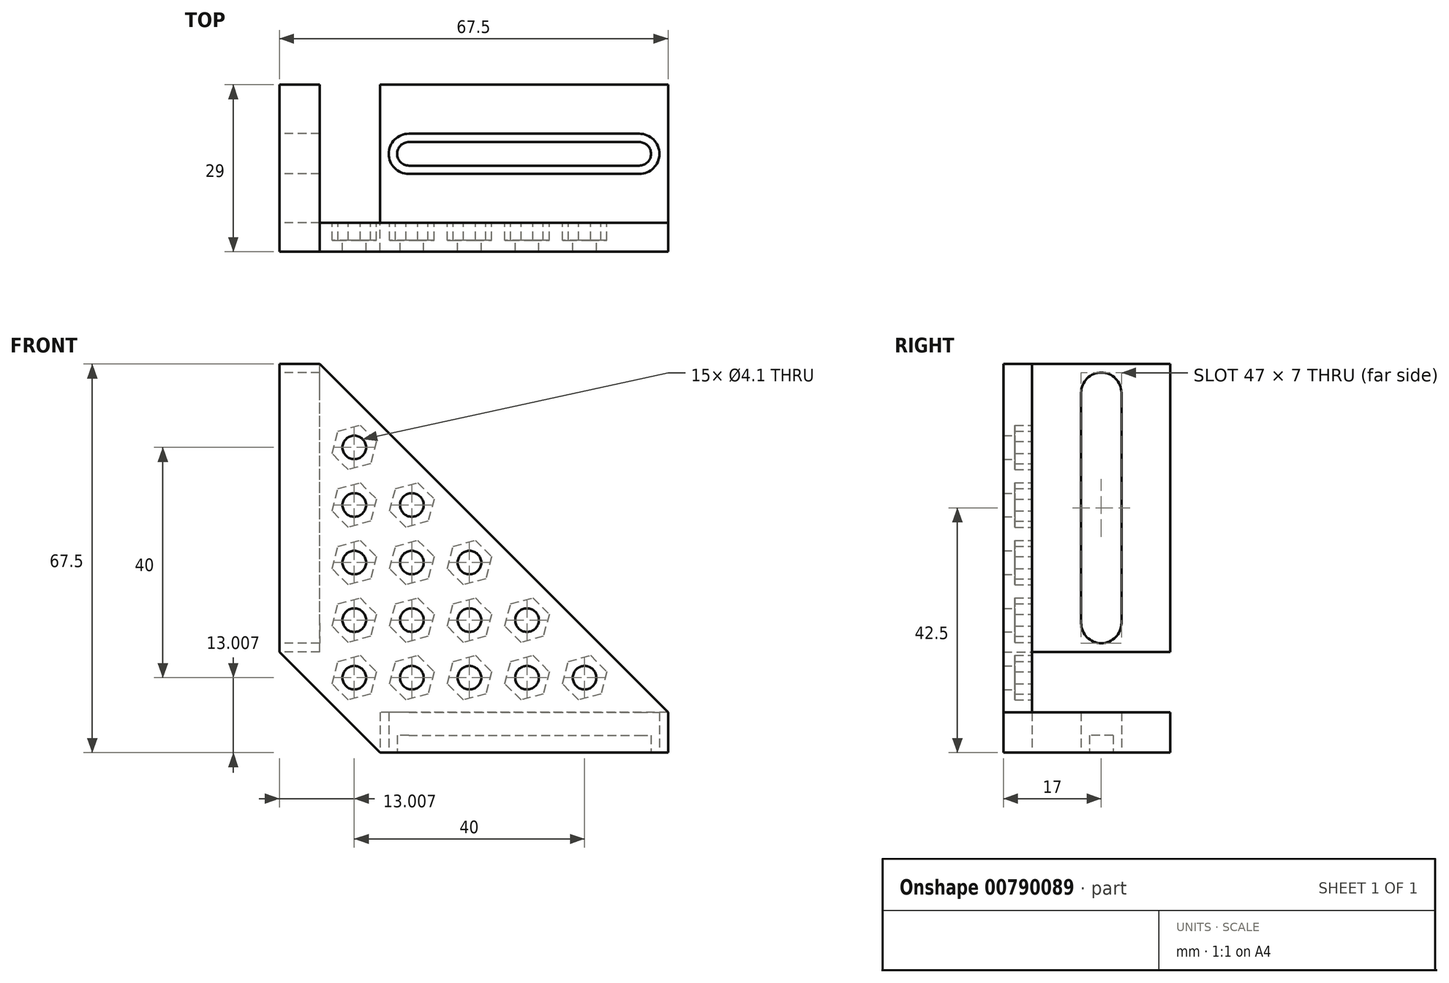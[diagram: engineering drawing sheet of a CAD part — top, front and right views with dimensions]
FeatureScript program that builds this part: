
annotation { "Feature Type Name" : "Feature", "Feature Type Description" : "" }
export const myFeature = defineFeature(function(context is Context, id is Id, definition is map)
    precondition{}
    {
        {
            var Q0;
            Q0=qCreatedBy(makeId("Top.planeOp"),FACE);
            var sketch = newSketch(context, id + "F0", { "sketchPlane" : qUnion([Q0])});
            skLineSegment(sketch, "E0.left", {"start": v(-21, 12) * mm, "end": v(-21, -12) * mm});
            skPoint(sketch, "E0.middle", {"position": v(0, 0) * mm});
            skLineSegment(sketch, "E1", {"start": v(-16, 12) * mm, "end": v(-16, -12) * mm, "construction": true});
            skPoint(sketch, "E2", {"position": v(-16, -8) * mm});
            skPoint(sketch, "E3", {"position": v(0, -8) * mm});
            skPoint(sketch, "E4", {"position": v(-16, 0) * mm});
            skArc(sketch, "E5", {"start": v(-16, -5.95) * mm, "mid": v(-18.05, -8) * mm, "end": v(-16, -10.05) * mm});
            skLineSegment(sketch, "E6", {"start": v(-16, -5.95) * mm, "end": v(0, -5.95) * mm});
            skLineSegment(sketch, "E7.MirrorCS", {"start": v(-16, -10.05) * mm, "end": v(0, -10.05) * mm});
            skArc(sketch, "E8", {"start": v(-16, -2.05) * mm, "mid": v(-18.05, 0) * mm, "end": v(-16, 2.05) * mm});
            skLineSegment(sketch, "E9", {"start": v(-16, -2.05) * mm, "end": v(0, -2.05) * mm});
            skPoint(sketch, "E10.MirrorP", {"position": v(-16, 2.05) * mm});
            skLineSegment(sketch, "E11.MirrorCS", {"start": v(-16, 2.05) * mm, "end": v(0, 2.05) * mm});
            skLineSegment(sketch, "E12.MirrorCS", {"start": v(0, -12) * mm, "end": v(0, 12) * mm, "construction": true});
            skLineSegment(sketch, "E13", {"start": v(-21, -12) * mm, "end": v(0, -12) * mm});
            skLineSegment(sketch, "E14", {"start": v(-21, 0) * mm, "end": v(0, 0) * mm, "construction": true});
            skLineSegment(sketch, "E15", {"start": v(0, -8) * mm, "end": v(-21, -8) * mm, "construction": true});
            skPoint(sketch, "E15.endSnap0", {"position": v(-18.05, -8) * mm});
            skLineSegment(sketch, "E16", {"start": v(0, -12) * mm, "end": v(29, -12) * mm});
            skLineSegment(sketch, "E17", {"start": v(29, -12) * mm, "end": v(29, 12) * mm});
            skLineSegment(sketch, "E18", {"start": v(29, 12) * mm, "end": v(-21, 12) * mm});
            skLineSegment(sketch, "E19", {"start": v(24, 12) * mm, "end": v(24, -12) * mm, "construction": true});
            skLineSegment(sketch, "E20", {"start": v(0, -5.95) * mm, "end": v(24, -5.95) * mm});
            skLineSegment(sketch, "E21", {"start": v(0, -10.05) * mm, "end": v(24, -10.05) * mm});
            skLineSegment(sketch, "E22", {"start": v(0, -2.05) * mm, "end": v(24, -2.05) * mm});
            skLineSegment(sketch, "E23", {"start": v(0, 2.05) * mm, "end": v(24, 2.05) * mm});
            skLineSegment(sketch, "E24", {"start": v(24, 0) * mm, "end": v(0, 0) * mm, "construction": true});
            skLineSegment(sketch, "E25", {"start": v(0, -8) * mm, "end": v(24, -8) * mm, "construction": true});
            skArc(sketch, "E26", {"start": v(24, -2.05) * mm, "mid": v(26.05, 0) * mm, "end": v(24, 2.05) * mm});
            skArc(sketch, "E27", {"start": v(24, -10.05) * mm, "mid": v(26.05, -8) * mm, "end": v(24, -5.95) * mm});
            skLineSegment(sketch, "E28.MirrorCS", {"start": v(0, 5.95) * mm, "end": v(24, 5.95) * mm});
            skLineSegment(sketch, "E29.MirrorCS", {"start": v(0, 10.05) * mm, "end": v(24, 10.05) * mm});
            skLineSegment(sketch, "E30.MirrorCS", {"start": v(-16, 10.05) * mm, "end": v(0, 10.05) * mm});
            skLineSegment(sketch, "E31.MirrorCS", {"start": v(-16, 5.95) * mm, "end": v(0, 5.95) * mm});
            skArc(sketch, "E32.MirrorCS", {"start": v(-16, 5.95) * mm, "mid": v(-18.05, 8) * mm, "end": v(-16, 10.05) * mm});
            skArc(sketch, "E33.MirrorCS", {"start": v(24, 10.05) * mm, "mid": v(26.05, 8) * mm, "end": v(24, 5.95) * mm});
            skArc(sketch, "E34.0", {"start": v(-16, -3.5) * mm, "mid": v(-19.5, 0) * mm, "end": v(-16, 3.5) * mm});
            skLineSegment(sketch, "E34.1", {"start": v(0, 3.5) * mm, "end": v(24, 3.5) * mm});
            skArc(sketch, "E34.2", {"start": v(24, -3.5) * mm, "mid": v(27.5, 0) * mm, "end": v(24, 3.5) * mm});
            skLineSegment(sketch, "E34.3", {"start": v(-16, 3.5) * mm, "end": v(0, 3.5) * mm});
            skLineSegment(sketch, "E34.4", {"start": v(0, -3.5) * mm, "end": v(24, -3.5) * mm});
            skLineSegment(sketch, "E34.5", {"start": v(-16, -3.5) * mm, "end": v(0, -3.5) * mm});
            skArc(sketch, "E35.0", {"start": v(-16, -4.5) * mm, "mid": v(-19.5, -8) * mm, "end": v(-16, -11.5) * mm});
            skLineSegment(sketch, "E35.1", {"start": v(0, -4.5) * mm, "end": v(24, -4.5) * mm});
            skArc(sketch, "E35.2", {"start": v(24, -11.5) * mm, "mid": v(27.5, -8) * mm, "end": v(24, -4.5) * mm});
            skLineSegment(sketch, "E35.3", {"start": v(-16, -4.5) * mm, "end": v(0, -4.5) * mm});
            skLineSegment(sketch, "E35.4", {"start": v(0, -11.5) * mm, "end": v(24, -11.5) * mm});
            skLineSegment(sketch, "E35.5", {"start": v(-16, -11.5) * mm, "end": v(0, -11.5) * mm});
            skArc(sketch, "E36.0", {"start": v(-16, 4.5) * mm, "mid": v(-19.5, 8) * mm, "end": v(-16, 11.5) * mm});
            skLineSegment(sketch, "E36.1", {"start": v(0, 11.5) * mm, "end": v(24, 11.5) * mm});
            skArc(sketch, "E36.2", {"start": v(24, 11.5) * mm, "mid": v(27.5, 8) * mm, "end": v(24, 4.5) * mm});
            skLineSegment(sketch, "E36.3", {"start": v(-16, 11.5) * mm, "end": v(0, 11.5) * mm});
            skLineSegment(sketch, "E36.4", {"start": v(0, 4.5) * mm, "end": v(24, 4.5) * mm});
            skLineSegment(sketch, "E36.5", {"start": v(-16, 4.5) * mm, "end": v(0, 4.5) * mm});
            skSolve(sketch);
        }
        {
            var Q0;
            Q0=makeQuery(id+"F0.imprint","IMPRINT",FACE,{"disambiguationData":[TD([[makeQuery(id+"F0.imprint","IMPRINT",EDGE,{"derivedFrom":sQuery(id+"F0.wireOp",EDGE,"E0.left")}),1.0]])]});
            var Q1;
            Q1=makeQuery(id+"F0.imprint","IMPRINT",FACE,{"disambiguationData":[TD([[makeQuery(id+"F0.imprint","IMPRINT",EDGE,{"derivedFrom":sQuery(id+"F0.wireOp",EDGE,"E5")}),1.0]])]});
            var Q2;
            Q2=makeQuery(id+"F0.imprint","IMPRINT",FACE,{"disambiguationData":[TD([[makeQuery(id+"F0.imprint","IMPRINT",EDGE,{"derivedFrom":sQuery(id+"F0.wireOp",EDGE,"E5")}),-1.0]])]});
            var Q3;
            Q3=makeQuery(id+"F0.imprint","IMPRINT",FACE,{"disambiguationData":[TD([[makeQuery(id+"F0.imprint","IMPRINT",EDGE,{"derivedFrom":sQuery(id+"F0.wireOp",EDGE,"E28.MirrorCS")}),-1.0]])]});
            var Q4;
            Q4=makeQuery(id+"F0.imprint","IMPRINT",FACE,{"disambiguationData":[TD([[makeQuery(id+"F0.imprint","IMPRINT",EDGE,{"derivedFrom":sQuery(id+"F0.wireOp",EDGE,"E28.MirrorCS")}),1.0]])]});
            extrude(context, id + "F1", {"entities" : qUnion([Q0, Q1, Q2, Q3, Q4]), "depth" : 7 * mm, "offsetDistance" : 25 * mm});
        }
        {
            var Q0;
            Q0=makeQuery(id+"F0.imprint","IMPRINT",FACE,{"disambiguationData":[TD([[makeQuery(id+"F0.imprint","IMPRINT",EDGE,{"derivedFrom":sQuery(id+"F0.wireOp",EDGE,"E8")}),1.0]])]});
            extrude(context, id + "F2", {"entities" : qUnion([Q0]), "operationType" : NewBodyOperationType.ADD, "depth" : 3 * mm, "offsetDistance" : 25 * mm});
        }
        {
            var Q0;
            Q0=makeQuery(id+"F1.opExtrude","SWEPT_FACE",FACE,{"disambiguationData":[OSD([sQuery(id+"F0.wireOp",EDGE,"E0.left")])]});
            var sketch = newSketch(context, id + "F3", { "sketchPlane" : qUnion([Q0])});
            skLineSegment(sketch, "E37", {"start": v(-12, 3.5) * mm, "end": v(12, 3.5) * mm, "construction": true});
            skSolve(sketch);
        }
        {
            var Q0;
            Q0=makeQuery(id+"F1.opExtrude","SWEPT_BODY",BODY,{"disambiguationData":[OSD([sQuery(id+"F0.wireOp",EDGE,"E0.bottom"),sQuery(id+"F0.wireOp",EDGE,"E0.top"),sQuery(id+"F0.wireOp",EDGE,"E0.left"),sQuery(id+"F0.wireOp",EDGE,"E0.right"),sQuery(id+"F0.wireOp",EDGE,"rf366HtQ-3S43-huQP-rZQL-GLvETnePYKPt"),sQuery(id+"F0.wireOp",EDGE,"72d57c59-205e-4b86-9b7f-fefa83471a3c0.MirrorC"),sQuery(id+"F0.wireOp",EDGE,"3BxVGwLA-TLUy-tZVP-cH0U-NxRYkcQ5ksQi"),sQuery(id+"F0.wireOp",EDGE,"b526d6a5-a937-4610-9a53-f8e406b30c9d0.MirrorC"),sQuery(id+"F0.wireOp",EDGE,"71981b63-6e51-433c-862b-60b74b25135c0.MirrorC"),sQuery(id+"F0.wireOp",EDGE,"b5f8f83e-67df-48da-9f18-6f8bbd20fa1b0.MirrorC"),sQuery(id+"F0.wireOp",EDGE,"1DxgEhBs-8iCY-IMLj-HmtB-05ri525AO9wY"),sQuery(id+"F0.wireOp",EDGE,"NxLUD5A4-VjtB-lD8M-x3iM-VxBEk0lLSaKk"),sQuery(id+"F0.wireOp",EDGE,"3f1f5e11-1e70-4af8-87df-d7b5c765f6460.MirrorC")])]});
            var Q1;
            Q1=sQuery(id+"F3.wireOp",EDGE,"E37");
            transform(context, id + "F4", {"entities" : qUnion([Q0]), "transformType" : TransformType.ROTATION, "transformAxis" : qUnion([Q1]), "angle" : 90 * degree, "makeCopy" : true});
        }
        {
            var Q0;
            Q0=makeQuery(id+"F4.opPattern","COPY",FACE,{"derivedFrom":makeQuery(id+"F1.opExtrude","SWEPT_FACE",FACE,{"disambiguationData":[OSD([sQuery(id+"F0.wireOp",EDGE,"E0.left")])]}),"instanceName":"1"});
            var sketch = newSketch(context, id + "F5", { "sketchPlane" : qUnion([Q0])});
            skLineSegment(sketch, "E38", {"start": v(-21, -12) * mm, "end": v(-21, 12) * mm, "construction": true});
            skPoint(sketch, "E38.startSnap0", {"position": v(-21, -12) * mm});
            skSolve(sketch);
        }
        {
            var Q0;
            Q0=sQuery(id+"F5.wireOp",EDGE,"E38");
            cPlane(context, id + "F6", {"entities" : qUnion([Q0]), "cplaneType" : CPlaneType.LINE_ANGLE, "offset" : 25 * mm, "angle" : 90 * degree, "width" : 150 * mm, "height" : 150 * mm});
        }
        {
            var Q0;
            Q0=qCreatedBy(id+"F6.planeOp",FACE);
            var sketch = newSketch(context, id + "F7", { "sketchPlane" : qUnion([Q0])});
            skLineSegment(sketch, "E39", {"start": v(0, 3.5) * mm, "end": v(0, 53.5) * mm, "construction": true});
            skSolve(sketch);
        }
        {
            var Q0;
            Q0=makeQuery(id+"F4.opPattern","COPY",BODY,{"derivedFrom":makeQuery(id+"F1.opExtrude","SWEPT_BODY",BODY,{"disambiguationData":[OSD([sQuery(id+"F0.wireOp",EDGE,"E0.left"),sQuery(id+"F0.wireOp",EDGE,"E13"),sQuery(id+"F0.wireOp",EDGE,"E16"),sQuery(id+"F0.wireOp",EDGE,"E17"),sQuery(id+"F0.wireOp",EDGE,"E18"),sQuery(id+"F0.wireOp",EDGE,"E34.0"),sQuery(id+"F0.wireOp",EDGE,"E34.1"),sQuery(id+"F0.wireOp",EDGE,"E34.2"),sQuery(id+"F0.wireOp",EDGE,"E34.3"),sQuery(id+"F0.wireOp",EDGE,"E34.4"),sQuery(id+"F0.wireOp",EDGE,"E34.5")])]}),"instanceName":"1"});
            var Q1;
            Q1=sQuery(id+"F7.wireOp",EDGE,"E39");
            transform(context, id + "F8", {"entities" : qUnion([Q0]), "transformType" : TransformType.ROTATION, "transformAxis" : qUnion([Q1]), "angle" : 180 * degree, "makeCopy" : false});
        }
        {
            var Q0;
            Q0=makeQuery(id+"F4.opPattern","COPY",BODY,{"derivedFrom":makeQuery(id+"F1.opExtrude","SWEPT_BODY",BODY,{"disambiguationData":[OSD([sQuery(id+"F0.wireOp",EDGE,"E0.bottom"),sQuery(id+"F0.wireOp",EDGE,"E0.top"),sQuery(id+"F0.wireOp",EDGE,"E0.left"),sQuery(id+"F0.wireOp",EDGE,"E0.right"),sQuery(id+"F0.wireOp",EDGE,"rf366HtQ-3S43-huQP-rZQL-GLvETnePYKPt"),sQuery(id+"F0.wireOp",EDGE,"72d57c59-205e-4b86-9b7f-fefa83471a3c0.MirrorC"),sQuery(id+"F0.wireOp",EDGE,"3BxVGwLA-TLUy-tZVP-cH0U-NxRYkcQ5ksQi"),sQuery(id+"F0.wireOp",EDGE,"b526d6a5-a937-4610-9a53-f8e406b30c9d0.MirrorC"),sQuery(id+"F0.wireOp",EDGE,"71981b63-6e51-433c-862b-60b74b25135c0.MirrorC"),sQuery(id+"F0.wireOp",EDGE,"b5f8f83e-67df-48da-9f18-6f8bbd20fa1b0.MirrorC"),sQuery(id+"F0.wireOp",EDGE,"1DxgEhBs-8iCY-IMLj-HmtB-05ri525AO9wY"),sQuery(id+"F0.wireOp",EDGE,"NxLUD5A4-VjtB-lD8M-x3iM-VxBEk0lLSaKk"),sQuery(id+"F0.wireOp",EDGE,"3f1f5e11-1e70-4af8-87df-d7b5c765f6460.MirrorC")])]}),"instanceName":"1"});
            var Q1;
            Q1=qCreatedBy(makeId("Top.planeOp"),FACE);
            transform(context, id + "F9", {"entities" : qUnion([Q0]), "transformType" : TransformType.TRANSLATION_DISTANCE, "transformDirection" : qUnion([Q1]), "distance" : 14 * mm, "makeCopy" : false});
        }
        {
            var Q0;
            Q0=makeQuery(id+"F4.opPattern","COPY",BODY,{"derivedFrom":makeQuery(id+"F1.opExtrude","SWEPT_BODY",BODY,{"disambiguationData":[OSD([sQuery(id+"F0.wireOp",EDGE,"E0.bottom"),sQuery(id+"F0.wireOp",EDGE,"E0.top"),sQuery(id+"F0.wireOp",EDGE,"E0.left"),sQuery(id+"F0.wireOp",EDGE,"E0.right"),sQuery(id+"F0.wireOp",EDGE,"rf366HtQ-3S43-huQP-rZQL-GLvETnePYKPt"),sQuery(id+"F0.wireOp",EDGE,"72d57c59-205e-4b86-9b7f-fefa83471a3c0.MirrorC"),sQuery(id+"F0.wireOp",EDGE,"3BxVGwLA-TLUy-tZVP-cH0U-NxRYkcQ5ksQi"),sQuery(id+"F0.wireOp",EDGE,"b526d6a5-a937-4610-9a53-f8e406b30c9d0.MirrorC"),sQuery(id+"F0.wireOp",EDGE,"71981b63-6e51-433c-862b-60b74b25135c0.MirrorC"),sQuery(id+"F0.wireOp",EDGE,"b5f8f83e-67df-48da-9f18-6f8bbd20fa1b0.MirrorC"),sQuery(id+"F0.wireOp",EDGE,"1DxgEhBs-8iCY-IMLj-HmtB-05ri525AO9wY"),sQuery(id+"F0.wireOp",EDGE,"NxLUD5A4-VjtB-lD8M-x3iM-VxBEk0lLSaKk"),sQuery(id+"F0.wireOp",EDGE,"3f1f5e11-1e70-4af8-87df-d7b5c765f6460.MirrorC")])]}),"instanceName":"1"});
            var Q1;
            Q1=qCreatedBy(makeId("Right.planeOp"),FACE);
            transform(context, id + "F10", {"entities" : qUnion([Q0]), "transformType" : TransformType.TRANSLATION_DISTANCE, "transformDirection" : qUnion([Q1]), "distance" : 14 * mm, "oppositeDirection" : true, "makeCopy" : false});
        }
        {
            var Q0;
            Q0=sQuery(id+"F0.wireOp",VERTEX,"E0.left.end");
            var Q1;
            Q1=makeQuery(id+"F4.opPattern","COPY",VERTEX,{"derivedFrom":makeQuery(id+"F1.opExtrude","CAP_VERTEX",VERTEX,{"disambiguationData":[OSD([sQuery(id+"F0.wireOp",EDGE,"E0.left"),sQuery(id+"F0.wireOp",EDGE,"E18")])],"isStart":true}),"instanceName":"1"});
            var Q2;
            Q2=makeQuery(id+"F4.opPattern","COPY",VERTEX,{"derivedFrom":makeQuery(id+"F1.opExtrude","CAP_VERTEX",VERTEX,{"disambiguationData":[OSD([sQuery(id+"F0.wireOp",EDGE,"E0.left"),sQuery(id+"F0.wireOp",EDGE,"E18")])],"isStart":false}),"instanceName":"1"});
            cPlane(context, id + "F11", {"entities" : qUnion([Q0, Q1, Q2]), "cplaneType" : CPlaneType.THREE_POINT, "offset" : 25 * mm, "width" : 150 * mm, "height" : 150 * mm});
        }
        {
            var Q0;
            Q0=qCreatedBy(id+"F11.planeOp",FACE);
            var sketch = newSketch(context, id + "F12", { "sketchPlane" : qUnion([Q0])});
            skLineSegment(sketch, "E40", {"start": v(-21, 0) * mm, "end": v(-38.5, 17.5) * mm});
            skLineSegment(sketch, "E41", {"start": v(-31.5, 67.5) * mm, "end": v(29, 7) * mm});
            skLineSegment(sketch, "E42", {"start": v(-38.5, 17.5) * mm, "end": v(-38.5, 67.5) * mm});
            skLineSegment(sketch, "E43", {"start": v(-31.5, 67.5) * mm, "end": v(-38.5, 67.5) * mm});
            skLineSegment(sketch, "E44", {"start": v(-21, 0) * mm, "end": v(29, 0) * mm});
            skLineSegment(sketch, "E45", {"start": v(29, 0) * mm, "end": v(29, 7) * mm});
            skLineSegment(sketch, "E46", {"start": v(-38.5, 67.5) * mm, "end": v(-31.5, 67.5) * mm});
            skPoint(sketch, "E47", {"position": v(-5.5, 33) * mm});
            skCircle(sketch, "E48", {"center": v(-5.5, 33) * mm, "radius": 2.05 * mm});
            skCircle(sketch, "E49.cCircle", {"center": v(-5.5, 33) * mm, "radius": 4 * mm, "construction": true});
            skLineSegment(sketch, "E49.0", {"start": v(-8.32, 35.84) * mm, "end": v(-4.46, 36.87) * mm});
            skLineSegment(sketch, "E49.1", {"start": v(-4.46, 36.87) * mm, "end": v(-1.63, 34.04) * mm});
            skLineSegment(sketch, "E49.2", {"start": v(-1.63, 34.04) * mm, "end": v(-2.66, 30.18) * mm});
            skLineSegment(sketch, "E49.3", {"start": v(-2.66, 30.18) * mm, "end": v(-6.53, 29.14) * mm});
            skLineSegment(sketch, "E49.4", {"start": v(-6.53, 29.14) * mm, "end": v(-9.36, 31.97) * mm});
            skLineSegment(sketch, "E49.5", {"start": v(-9.36, 31.97) * mm, "end": v(-8.32, 35.84) * mm});
            skLineSegment(sketch, "E50", {"start": v(-29.75, 8.75) * mm, "end": v(-1.25, 37.25) * mm, "construction": true});
            skLineSegment(sketch, "E51", {"start": v(-38.5, 17.5) * mm, "end": v(-38.5, 0) * mm, "construction": true});
            skLineSegment(sketch, "E52", {"start": v(-38.5, 0) * mm, "end": v(-21, 0) * mm, "construction": true});
            skLineSegment(sketch, "E53", {"start": v(-21, 7) * mm, "end": v(-38.5, 7) * mm, "construction": true});
            skLineSegment(sketch, "E54", {"start": v(-38.5, 7) * mm, "end": v(-38.5, 17.5) * mm, "construction": true});
            skLineSegment(sketch, "E55", {"start": v(-23.5, 59.5) * mm, "end": v(-23.5, 15) * mm, "construction": true});
            skLineSegment(sketch, "E56", {"start": v(-23.5, 15) * mm, "end": v(21, 15) * mm, "construction": true});
            skPoint(sketch, "E57", {"position": v(-2.66, 35.84) * mm});
            skLineSegment(sketch, "E58", {"start": v(-5.5, 33) * mm, "end": v(-5.5, 15) * mm, "construction": true});
            skLineSegment(sketch, "E59", {"start": v(-5.5, 33) * mm, "end": v(-23.5, 33) * mm, "construction": true});
            skPoint(sketch, "E60", {"position": v(-5.5, 23) * mm});
            skCircle(sketch, "E61", {"center": v(-5.5, 23) * mm, "radius": 2.05 * mm});
            skCircle(sketch, "E62.cCircle", {"center": v(-5.5, 23) * mm, "radius": 4 * mm, "construction": true});
            skLineSegment(sketch, "E62.0", {"start": v(-8.32, 25.84) * mm, "end": v(-4.46, 26.87) * mm});
            skLineSegment(sketch, "E62.1", {"start": v(-4.46, 26.87) * mm, "end": v(-1.63, 24.04) * mm});
            skLineSegment(sketch, "E62.2", {"start": v(-1.63, 24.04) * mm, "end": v(-2.66, 20.18) * mm});
            skLineSegment(sketch, "E62.3", {"start": v(-2.66, 20.18) * mm, "end": v(-6.53, 19.14) * mm});
            skLineSegment(sketch, "E62.4", {"start": v(-6.53, 19.14) * mm, "end": v(-9.36, 21.97) * mm});
            skLineSegment(sketch, "E62.5", {"start": v(-9.36, 21.97) * mm, "end": v(-8.32, 25.84) * mm});
            skPoint(sketch, "E63", {"position": v(-15.5, 33) * mm});
            skCircle(sketch, "E64", {"center": v(-15.5, 33) * mm, "radius": 2.05 * mm});
            skCircle(sketch, "E65.cCircle", {"center": v(-15.5, 33) * mm, "radius": 4 * mm, "construction": true});
            skLineSegment(sketch, "E65.0", {"start": v(-18.32, 35.84) * mm, "end": v(-14.46, 36.87) * mm});
            skLineSegment(sketch, "E65.1", {"start": v(-14.46, 36.87) * mm, "end": v(-11.63, 34.04) * mm});
            skLineSegment(sketch, "E65.2", {"start": v(-11.63, 34.04) * mm, "end": v(-12.66, 30.18) * mm});
            skLineSegment(sketch, "E65.3", {"start": v(-12.66, 30.18) * mm, "end": v(-16.53, 29.14) * mm});
            skLineSegment(sketch, "E65.4", {"start": v(-16.53, 29.14) * mm, "end": v(-19.36, 31.97) * mm});
            skLineSegment(sketch, "E65.5", {"start": v(-19.36, 31.97) * mm, "end": v(-18.32, 35.84) * mm});
            skPoint(sketch, "E66", {"position": v(-15.5, 23) * mm});
            skCircle(sketch, "E67", {"center": v(-15.5, 23) * mm, "radius": 2.05 * mm});
            skCircle(sketch, "E68.cCircle", {"center": v(-15.5, 23) * mm, "radius": 4 * mm, "construction": true});
            skLineSegment(sketch, "E68.0", {"start": v(-18.32, 25.84) * mm, "end": v(-14.46, 26.87) * mm});
            skLineSegment(sketch, "E68.1", {"start": v(-14.46, 26.87) * mm, "end": v(-11.63, 24.04) * mm});
            skLineSegment(sketch, "E68.2", {"start": v(-11.63, 24.04) * mm, "end": v(-12.66, 20.18) * mm});
            skLineSegment(sketch, "E68.3", {"start": v(-12.66, 20.18) * mm, "end": v(-16.53, 19.14) * mm});
            skLineSegment(sketch, "E68.4", {"start": v(-16.53, 19.14) * mm, "end": v(-19.36, 21.97) * mm});
            skLineSegment(sketch, "E68.5", {"start": v(-19.36, 21.97) * mm, "end": v(-18.32, 25.84) * mm});
            skLineSegment(sketch, "E69", {"start": v(-5.5, 23) * mm, "end": v(13, 23) * mm, "construction": true});
            skLineSegment(sketch, "E70", {"start": v(-15.5, 33) * mm, "end": v(-15.5, 51.5) * mm, "construction": true});
            skPoint(sketch, "E71", {"position": v(4.5, 23) * mm});
            skCircle(sketch, "E72", {"center": v(4.5, 23) * mm, "radius": 2.05 * mm});
            skCircle(sketch, "E73.cCircle", {"center": v(4.5, 23) * mm, "radius": 4 * mm, "construction": true});
            skLineSegment(sketch, "E73.0", {"start": v(1.68, 25.84) * mm, "end": v(5.54, 26.87) * mm});
            skLineSegment(sketch, "E73.1", {"start": v(5.54, 26.87) * mm, "end": v(8.37, 24.04) * mm});
            skLineSegment(sketch, "E73.2", {"start": v(8.37, 24.04) * mm, "end": v(7.34, 20.18) * mm});
            skLineSegment(sketch, "E73.3", {"start": v(7.34, 20.18) * mm, "end": v(3.47, 19.14) * mm});
            skLineSegment(sketch, "E73.4", {"start": v(3.47, 19.14) * mm, "end": v(0.64, 21.97) * mm});
            skLineSegment(sketch, "E73.5", {"start": v(0.64, 21.97) * mm, "end": v(1.68, 25.84) * mm});
            skPoint(sketch, "E74", {"position": v(-15.5, 43) * mm});
            skCircle(sketch, "E75", {"center": v(-15.5, 43) * mm, "radius": 2.05 * mm});
            skCircle(sketch, "E76.cCircle", {"center": v(-15.5, 43) * mm, "radius": 4 * mm, "construction": true});
            skLineSegment(sketch, "E76.0", {"start": v(-18.32, 45.84) * mm, "end": v(-14.46, 46.87) * mm});
            skLineSegment(sketch, "E76.1", {"start": v(-14.46, 46.87) * mm, "end": v(-11.63, 44.04) * mm});
            skLineSegment(sketch, "E76.2", {"start": v(-11.63, 44.04) * mm, "end": v(-12.66, 40.18) * mm});
            skLineSegment(sketch, "E76.3", {"start": v(-12.66, 40.18) * mm, "end": v(-16.53, 39.14) * mm});
            skLineSegment(sketch, "E76.4", {"start": v(-16.53, 39.14) * mm, "end": v(-19.36, 41.97) * mm});
            skLineSegment(sketch, "E76.5", {"start": v(-19.36, 41.97) * mm, "end": v(-18.32, 45.84) * mm});
            skPoint(sketch, "E77", {"position": v(-25.5, 33) * mm});
            skCircle(sketch, "E78", {"center": v(-25.5, 33) * mm, "radius": 2.05 * mm});
            skCircle(sketch, "E79.cCircle", {"center": v(-25.5, 33) * mm, "radius": 4 * mm, "construction": true});
            skLineSegment(sketch, "E79.0", {"start": v(-28.32, 35.84) * mm, "end": v(-24.46, 36.87) * mm});
            skLineSegment(sketch, "E79.1", {"start": v(-24.46, 36.87) * mm, "end": v(-21.63, 34.04) * mm});
            skLineSegment(sketch, "E79.2", {"start": v(-21.63, 34.04) * mm, "end": v(-22.66, 30.18) * mm});
            skLineSegment(sketch, "E79.3", {"start": v(-22.66, 30.18) * mm, "end": v(-26.53, 29.14) * mm});
            skLineSegment(sketch, "E79.4", {"start": v(-26.53, 29.14) * mm, "end": v(-29.36, 31.97) * mm});
            skLineSegment(sketch, "E79.5", {"start": v(-29.36, 31.97) * mm, "end": v(-28.32, 35.84) * mm});
            skPoint(sketch, "E80", {"position": v(-25.5, 23) * mm});
            skCircle(sketch, "E81", {"center": v(-25.5, 23) * mm, "radius": 2.05 * mm});
            skCircle(sketch, "E82.cCircle", {"center": v(-25.5, 23) * mm, "radius": 4 * mm, "construction": true});
            skLineSegment(sketch, "E82.0", {"start": v(-28.32, 25.84) * mm, "end": v(-24.46, 26.87) * mm});
            skLineSegment(sketch, "E82.1", {"start": v(-24.46, 26.87) * mm, "end": v(-21.63, 24.04) * mm});
            skLineSegment(sketch, "E82.2", {"start": v(-21.63, 24.04) * mm, "end": v(-22.66, 20.18) * mm});
            skLineSegment(sketch, "E82.3", {"start": v(-22.66, 20.18) * mm, "end": v(-26.53, 19.14) * mm});
            skLineSegment(sketch, "E82.4", {"start": v(-26.53, 19.14) * mm, "end": v(-29.36, 21.97) * mm});
            skLineSegment(sketch, "E82.5", {"start": v(-29.36, 21.97) * mm, "end": v(-28.32, 25.84) * mm});
            skPoint(sketch, "E83", {"position": v(-25.5, 43) * mm});
            skCircle(sketch, "E84", {"center": v(-25.5, 43) * mm, "radius": 2.05 * mm});
            skCircle(sketch, "E85.cCircle", {"center": v(-25.5, 43) * mm, "radius": 4 * mm, "construction": true});
            skLineSegment(sketch, "E85.0", {"start": v(-28.32, 45.84) * mm, "end": v(-24.46, 46.87) * mm});
            skLineSegment(sketch, "E85.1", {"start": v(-24.46, 46.87) * mm, "end": v(-21.63, 44.04) * mm});
            skLineSegment(sketch, "E85.2", {"start": v(-21.63, 44.04) * mm, "end": v(-22.66, 40.18) * mm});
            skLineSegment(sketch, "E85.3", {"start": v(-22.66, 40.18) * mm, "end": v(-26.53, 39.14) * mm});
            skLineSegment(sketch, "E85.4", {"start": v(-26.53, 39.14) * mm, "end": v(-29.36, 41.97) * mm});
            skLineSegment(sketch, "E85.5", {"start": v(-29.36, 41.97) * mm, "end": v(-28.32, 45.84) * mm});
            skLineSegment(sketch, "E86", {"start": v(-25.5, 61.5) * mm, "end": v(-25.5, 13) * mm, "construction": true});
            skPoint(sketch, "E87", {"position": v(-5.5, 13) * mm});
            skCircle(sketch, "E88", {"center": v(-5.5, 13) * mm, "radius": 2.05 * mm});
            skCircle(sketch, "E89.cCircle", {"center": v(-5.5, 13) * mm, "radius": 4 * mm, "construction": true});
            skLineSegment(sketch, "E89.0", {"start": v(-8.32, 15.84) * mm, "end": v(-4.46, 16.87) * mm});
            skLineSegment(sketch, "E89.1", {"start": v(-4.46, 16.87) * mm, "end": v(-1.63, 14.04) * mm});
            skLineSegment(sketch, "E89.2", {"start": v(-1.63, 14.04) * mm, "end": v(-2.66, 10.18) * mm});
            skLineSegment(sketch, "E89.3", {"start": v(-2.66, 10.18) * mm, "end": v(-6.53, 9.14) * mm});
            skLineSegment(sketch, "E89.4", {"start": v(-6.53, 9.14) * mm, "end": v(-9.36, 11.97) * mm});
            skLineSegment(sketch, "E89.5", {"start": v(-9.36, 11.97) * mm, "end": v(-8.32, 15.84) * mm});
            skPoint(sketch, "E90", {"position": v(-15.5, 13) * mm});
            skCircle(sketch, "E91", {"center": v(-15.5, 13) * mm, "radius": 2.05 * mm});
            skCircle(sketch, "E92.cCircle", {"center": v(-15.5, 13) * mm, "radius": 4 * mm, "construction": true});
            skLineSegment(sketch, "E92.0", {"start": v(-18.32, 15.84) * mm, "end": v(-14.46, 16.87) * mm});
            skLineSegment(sketch, "E92.1", {"start": v(-14.46, 16.87) * mm, "end": v(-11.63, 14.04) * mm});
            skLineSegment(sketch, "E92.2", {"start": v(-11.63, 14.04) * mm, "end": v(-12.66, 10.18) * mm});
            skLineSegment(sketch, "E92.3", {"start": v(-12.66, 10.18) * mm, "end": v(-16.53, 9.14) * mm});
            skLineSegment(sketch, "E92.4", {"start": v(-16.53, 9.14) * mm, "end": v(-19.36, 11.97) * mm});
            skLineSegment(sketch, "E92.5", {"start": v(-19.36, 11.97) * mm, "end": v(-18.32, 15.84) * mm});
            skPoint(sketch, "E93", {"position": v(4.5, 13) * mm});
            skCircle(sketch, "E94", {"center": v(4.5, 13) * mm, "radius": 2.05 * mm});
            skCircle(sketch, "E95.cCircle", {"center": v(4.5, 13) * mm, "radius": 4 * mm, "construction": true});
            skLineSegment(sketch, "E95.0", {"start": v(1.68, 15.84) * mm, "end": v(5.54, 16.87) * mm});
            skLineSegment(sketch, "E95.1", {"start": v(5.54, 16.87) * mm, "end": v(8.37, 14.04) * mm});
            skLineSegment(sketch, "E95.2", {"start": v(8.37, 14.04) * mm, "end": v(7.34, 10.18) * mm});
            skLineSegment(sketch, "E95.3", {"start": v(7.34, 10.18) * mm, "end": v(3.47, 9.14) * mm});
            skLineSegment(sketch, "E95.4", {"start": v(3.47, 9.14) * mm, "end": v(0.64, 11.97) * mm});
            skLineSegment(sketch, "E95.5", {"start": v(0.64, 11.97) * mm, "end": v(1.68, 15.84) * mm});
            skPoint(sketch, "E96", {"position": v(-25.5, 13) * mm});
            skCircle(sketch, "E97", {"center": v(-25.5, 13) * mm, "radius": 2.05 * mm});
            skCircle(sketch, "E98.cCircle", {"center": v(-25.5, 13) * mm, "radius": 4 * mm, "construction": true});
            skLineSegment(sketch, "E98.0", {"start": v(-28.32, 15.84) * mm, "end": v(-24.46, 16.87) * mm});
            skLineSegment(sketch, "E98.1", {"start": v(-24.46, 16.87) * mm, "end": v(-21.63, 14.04) * mm});
            skLineSegment(sketch, "E98.2", {"start": v(-21.63, 14.04) * mm, "end": v(-22.66, 10.18) * mm});
            skLineSegment(sketch, "E98.3", {"start": v(-22.66, 10.18) * mm, "end": v(-26.53, 9.14) * mm});
            skLineSegment(sketch, "E98.4", {"start": v(-26.53, 9.14) * mm, "end": v(-29.36, 11.97) * mm});
            skLineSegment(sketch, "E98.5", {"start": v(-29.36, 11.97) * mm, "end": v(-28.32, 15.84) * mm});
            skLineSegment(sketch, "E99", {"start": v(23, 13) * mm, "end": v(-25.5, 13) * mm, "construction": true});
            skPoint(sketch, "E100", {"position": v(-25.5, 53) * mm});
            skCircle(sketch, "E101", {"center": v(-25.5, 53) * mm, "radius": 2.05 * mm});
            skCircle(sketch, "E102.cCircle", {"center": v(-25.5, 53) * mm, "radius": 4 * mm, "construction": true});
            skLineSegment(sketch, "E102.0", {"start": v(-29.36, 51.97) * mm, "end": v(-28.32, 55.84) * mm});
            skLineSegment(sketch, "E102.1", {"start": v(-28.32, 55.84) * mm, "end": v(-24.46, 56.87) * mm});
            skLineSegment(sketch, "E102.2", {"start": v(-24.46, 56.87) * mm, "end": v(-21.63, 54.04) * mm});
            skLineSegment(sketch, "E102.3", {"start": v(-21.63, 54.04) * mm, "end": v(-22.66, 50.18) * mm});
            skLineSegment(sketch, "E102.4", {"start": v(-22.66, 50.18) * mm, "end": v(-26.53, 49.14) * mm});
            skLineSegment(sketch, "E102.5", {"start": v(-26.53, 49.14) * mm, "end": v(-29.36, 51.97) * mm});
            skPoint(sketch, "E103", {"position": v(14.5, 13) * mm});
            skCircle(sketch, "E104", {"center": v(14.5, 13) * mm, "radius": 2.05 * mm});
            skCircle(sketch, "E105.cCircle", {"center": v(14.5, 13) * mm, "radius": 4 * mm, "construction": true});
            skLineSegment(sketch, "E105.0", {"start": v(11.68, 15.84) * mm, "end": v(15.54, 16.87) * mm});
            skLineSegment(sketch, "E105.1", {"start": v(15.54, 16.87) * mm, "end": v(18.37, 14.04) * mm});
            skLineSegment(sketch, "E105.2", {"start": v(18.37, 14.04) * mm, "end": v(17.34, 10.18) * mm});
            skLineSegment(sketch, "E105.3", {"start": v(17.34, 10.18) * mm, "end": v(13.47, 9.14) * mm});
            skLineSegment(sketch, "E105.4", {"start": v(13.47, 9.14) * mm, "end": v(10.64, 11.97) * mm});
            skLineSegment(sketch, "E105.5", {"start": v(10.64, 11.97) * mm, "end": v(11.68, 15.84) * mm});
            skSolve(sketch);
        }
        {
            var Q0;
            Q0=makeQuery(id+"F12.imprint","IMPRINT",FACE,{"disambiguationData":[TD([[makeQuery(id+"F12.imprint","IMPRINT",EDGE,{"derivedFrom":sQuery(id+"F12.wireOp",EDGE,"E41")}),-1.0]])]});
            var Q1;
            Q1=makeQuery(id+"F12.imprint","IMPRINT",FACE,{"disambiguationData":[TD([[makeQuery(id+"F12.imprint","IMPRINT",EDGE,{"derivedFrom":sQuery(id+"F12.wireOp",EDGE,"544cc5c5-56e9-462e-aa7d-0e891712fb88")}),-1.0]])]});
            var Q2;
            Q2=makeQuery(id+"F12.imprint","IMPRINT",FACE,{"disambiguationData":[TD([[makeQuery(id+"F12.imprint","IMPRINT",EDGE,{"derivedFrom":sQuery(id+"F12.wireOp",EDGE,"af930993-f983-4d4b-806c-d5d714f01deb")}),-1.0]])]});
            var Q3;
            Q3=makeQuery(id+"F12.imprint","IMPRINT",FACE,{"disambiguationData":[TD([[makeQuery(id+"F12.imprint","IMPRINT",EDGE,{"derivedFrom":sQuery(id+"F12.wireOp",EDGE,"E48")}),-1.0]])]});
            var Q4;
            Q4=makeQuery(id+"F12.imprint","IMPRINT",FACE,{"disambiguationData":[TD([[makeQuery(id+"F12.imprint","IMPRINT",EDGE,{"derivedFrom":sQuery(id+"F12.wireOp",EDGE,"db4000d2-28b7-4ce0-b6f8-efe2c8e47721")}),-1.0]])]});
            var Q5;
            Q5=makeQuery(id+"F12.imprint","IMPRINT",FACE,{"disambiguationData":[TD([[makeQuery(id+"F12.imprint","IMPRINT",EDGE,{"derivedFrom":sQuery(id+"F12.wireOp",EDGE,"6fd45c98-9014-41e2-a4b9-07c20c1fc8f4")}),-1.0]])]});
            var Q6;
            {var subQ0=sQuery(id+"F12.wireOp",EDGE,"36f95dd1-a930-4b05-802e-2328d4aa170c.1");Q6=makeQuery(id+"F12.imprint","IMPRINT",FACE,{"disambiguationData":[TD([[makeQuery(id+"F12.imprint","IMPRINT",EDGE,{"derivedFrom":subQ0}),-1.0]])]});}
            var Q7;
            Q7=makeQuery(id+"F12.imprint","IMPRINT",FACE,{"disambiguationData":[TD([[makeQuery(id+"F12.imprint","IMPRINT",EDGE,{"derivedFrom":sQuery(id+"F12.wireOp",EDGE,"0217be3f-f015-4376-87de-3fac7a7125e00.MirrorCS")}),1.0]])]});
            var Q8;
            Q8=makeQuery(id+"F12.imprint","IMPRINT",FACE,{"disambiguationData":[TD([[makeQuery(id+"F12.imprint","IMPRINT",EDGE,{"derivedFrom":sQuery(id+"F12.wireOp",EDGE,"3a05cbfe-0b2f-41ad-9fce-b7c3e8f461170.MirrorCS")}),1.0]])]});
            var Q9;
            Q9=makeQuery(id+"F12.imprint","IMPRINT",FACE,{"disambiguationData":[TD([[makeQuery(id+"F12.imprint","IMPRINT",EDGE,{"derivedFrom":sQuery(id+"F12.wireOp",EDGE,"686798c7-8504-4800-9966-571d6854760d0.MirrorCS")}),1.0]])]});
            var Q10;
            Q10=makeQuery(id+"F12.imprint","IMPRINT",FACE,{"disambiguationData":[TD([[makeQuery(id+"F12.imprint","IMPRINT",EDGE,{"derivedFrom":sQuery(id+"F12.wireOp",EDGE,"ee1293b9-60a1-4feb-baa6-848b5ec06ea80.MirrorCS")}),1.0]])]});
            var Q11;
            Q11=makeQuery(id+"F12.imprint","IMPRINT",FACE,{"disambiguationData":[TD([[makeQuery(id+"F12.imprint","IMPRINT",EDGE,{"derivedFrom":sQuery(id+"F12.wireOp",EDGE,"E75")}),-1.0]])]});
            var Q12;
            Q12=makeQuery(id+"F12.imprint","IMPRINT",FACE,{"disambiguationData":[TD([[makeQuery(id+"F12.imprint","IMPRINT",EDGE,{"derivedFrom":sQuery(id+"F12.wireOp",EDGE,"E64")}),-1.0]])]});
            var Q13;
            Q13=makeQuery(id+"F12.imprint","IMPRINT",FACE,{"disambiguationData":[TD([[makeQuery(id+"F12.imprint","IMPRINT",EDGE,{"derivedFrom":sQuery(id+"F12.wireOp",EDGE,"E67")}),-1.0]])]});
            var Q14;
            Q14=makeQuery(id+"F12.imprint","IMPRINT",FACE,{"disambiguationData":[TD([[makeQuery(id+"F12.imprint","IMPRINT",EDGE,{"derivedFrom":sQuery(id+"F12.wireOp",EDGE,"E61")}),-1.0]])]});
            var Q15;
            Q15=makeQuery(id+"F12.imprint","IMPRINT",FACE,{"disambiguationData":[TD([[makeQuery(id+"F12.imprint","IMPRINT",EDGE,{"derivedFrom":sQuery(id+"F12.wireOp",EDGE,"E72")}),-1.0]])]});
            var Q16;
            Q16=makeQuery(id+"F12.imprint","IMPRINT",FACE,{"disambiguationData":[TD([[makeQuery(id+"F12.imprint","IMPRINT",EDGE,{"derivedFrom":sQuery(id+"F12.wireOp",EDGE,"E101")}),-1.0]])]});
            var Q17;
            Q17=makeQuery(id+"F12.imprint","IMPRINT",FACE,{"disambiguationData":[TD([[makeQuery(id+"F12.imprint","IMPRINT",EDGE,{"derivedFrom":sQuery(id+"F12.wireOp",EDGE,"E84")}),-1.0]])]});
            var Q18;
            Q18=makeQuery(id+"F12.imprint","IMPRINT",FACE,{"disambiguationData":[TD([[makeQuery(id+"F12.imprint","IMPRINT",EDGE,{"derivedFrom":sQuery(id+"F12.wireOp",EDGE,"E78")}),-1.0]])]});
            var Q19;
            Q19=makeQuery(id+"F12.imprint","IMPRINT",FACE,{"disambiguationData":[TD([[makeQuery(id+"F12.imprint","IMPRINT",EDGE,{"derivedFrom":sQuery(id+"F12.wireOp",EDGE,"E81")}),-1.0]])]});
            var Q20;
            Q20=makeQuery(id+"F12.imprint","IMPRINT",FACE,{"disambiguationData":[TD([[makeQuery(id+"F12.imprint","IMPRINT",EDGE,{"derivedFrom":sQuery(id+"F12.wireOp",EDGE,"E97")}),-1.0]])]});
            var Q21;
            Q21=makeQuery(id+"F12.imprint","IMPRINT",FACE,{"disambiguationData":[TD([[makeQuery(id+"F12.imprint","IMPRINT",EDGE,{"derivedFrom":sQuery(id+"F12.wireOp",EDGE,"E91")}),-1.0]])]});
            var Q22;
            Q22=makeQuery(id+"F12.imprint","IMPRINT",FACE,{"disambiguationData":[TD([[makeQuery(id+"F12.imprint","IMPRINT",EDGE,{"derivedFrom":sQuery(id+"F12.wireOp",EDGE,"E88")}),-1.0]])]});
            var Q23;
            Q23=makeQuery(id+"F12.imprint","IMPRINT",FACE,{"disambiguationData":[TD([[makeQuery(id+"F12.imprint","IMPRINT",EDGE,{"derivedFrom":sQuery(id+"F12.wireOp",EDGE,"E94")}),-1.0]])]});
            var Q24;
            Q24=makeQuery(id+"F12.imprint","IMPRINT",FACE,{"disambiguationData":[TD([[makeQuery(id+"F12.imprint","IMPRINT",EDGE,{"derivedFrom":sQuery(id+"F12.wireOp",EDGE,"E104")}),-1.0]])]});
            extrude(context, id + "F13", {"entities" : qUnion([Q0, Q1, Q2, Q3, Q4, Q5, Q6, Q7, Q8, Q9, Q10, Q11, Q12, Q13, Q14, Q15, Q16, Q17, Q18, Q19, Q20, Q21, Q22, Q23, Q24]), "operationType" : NewBodyOperationType.ADD, "depth" : 5 * mm, "offsetDistance" : 25 * mm});
        }
        {
            var Q0;
            Q0=makeQuery(id+"F12.imprint","IMPRINT",FACE,{"disambiguationData":[TD([[makeQuery(id+"F12.imprint","IMPRINT",EDGE,{"derivedFrom":sQuery(id+"F12.wireOp",EDGE,"E48")}),-1.0]])]});
            var Q1;
            Q1=makeQuery(id+"F12.imprint","IMPRINT",FACE,{"disambiguationData":[TD([[makeQuery(id+"F12.imprint","IMPRINT",EDGE,{"derivedFrom":sQuery(id+"F12.wireOp",EDGE,"af930993-f983-4d4b-806c-d5d714f01deb")}),-1.0]])]});
            var Q2;
            Q2=makeQuery(id+"F12.imprint","IMPRINT",FACE,{"disambiguationData":[TD([[makeQuery(id+"F12.imprint","IMPRINT",EDGE,{"derivedFrom":sQuery(id+"F12.wireOp",EDGE,"544cc5c5-56e9-462e-aa7d-0e891712fb88")}),-1.0]])]});
            var Q3;
            Q3=makeQuery(id+"F12.imprint","IMPRINT",FACE,{"disambiguationData":[TD([[makeQuery(id+"F12.imprint","IMPRINT",EDGE,{"derivedFrom":sQuery(id+"F12.wireOp",EDGE,"a7fd36b7-951d-469d-bd4a-abdf8a5abec4")}),-1.0]])]});
            var Q4;
            Q4=makeQuery(id+"F12.imprint","IMPRINT",FACE,{"disambiguationData":[TD([[makeQuery(id+"F12.imprint","IMPRINT",EDGE,{"derivedFrom":sQuery(id+"F12.wireOp",EDGE,"db4000d2-28b7-4ce0-b6f8-efe2c8e47721")}),-1.0]])]});
            var Q5;
            Q5=makeQuery(id+"F12.imprint","IMPRINT",FACE,{"disambiguationData":[TD([[makeQuery(id+"F12.imprint","IMPRINT",EDGE,{"derivedFrom":sQuery(id+"F12.wireOp",EDGE,"6fd45c98-9014-41e2-a4b9-07c20c1fc8f4")}),-1.0]])]});
            var Q6;
            Q6=makeQuery(id+"F12.imprint","IMPRINT",FACE,{"disambiguationData":[TD([[makeQuery(id+"F12.imprint","IMPRINT",EDGE,{"derivedFrom":sQuery(id+"F12.wireOp",EDGE,"0217be3f-f015-4376-87de-3fac7a7125e00.MirrorCS")}),1.0]])]});
            var Q7;
            Q7=makeQuery(id+"F12.imprint","IMPRINT",FACE,{"disambiguationData":[TD([[makeQuery(id+"F12.imprint","IMPRINT",EDGE,{"derivedFrom":sQuery(id+"F12.wireOp",EDGE,"3a05cbfe-0b2f-41ad-9fce-b7c3e8f461170.MirrorCS")}),1.0]])]});
            var Q8;
            Q8=makeQuery(id+"F12.imprint","IMPRINT",FACE,{"disambiguationData":[TD([[makeQuery(id+"F12.imprint","IMPRINT",EDGE,{"derivedFrom":sQuery(id+"F12.wireOp",EDGE,"686798c7-8504-4800-9966-571d6854760d0.MirrorCS")}),1.0]])]});
            var Q9;
            Q9=makeQuery(id+"F12.imprint","IMPRINT",FACE,{"disambiguationData":[TD([[makeQuery(id+"F12.imprint","IMPRINT",EDGE,{"derivedFrom":sQuery(id+"F12.wireOp",EDGE,"ee1293b9-60a1-4feb-baa6-848b5ec06ea80.MirrorCS")}),1.0]])]});
            var Q10;
            Q10=makeQuery(id+"F12.imprint","IMPRINT",FACE,{"disambiguationData":[TD([[makeQuery(id+"F12.imprint","IMPRINT",EDGE,{"derivedFrom":sQuery(id+"F12.wireOp",EDGE,"E72")}),-1.0]])]});
            var Q11;
            Q11=makeQuery(id+"F12.imprint","IMPRINT",FACE,{"disambiguationData":[TD([[makeQuery(id+"F12.imprint","IMPRINT",EDGE,{"derivedFrom":sQuery(id+"F12.wireOp",EDGE,"E61")}),-1.0]])]});
            var Q12;
            Q12=makeQuery(id+"F12.imprint","IMPRINT",FACE,{"disambiguationData":[TD([[makeQuery(id+"F12.imprint","IMPRINT",EDGE,{"derivedFrom":sQuery(id+"F12.wireOp",EDGE,"E67")}),-1.0]])]});
            var Q13;
            Q13=makeQuery(id+"F12.imprint","IMPRINT",FACE,{"disambiguationData":[TD([[makeQuery(id+"F12.imprint","IMPRINT",EDGE,{"derivedFrom":sQuery(id+"F12.wireOp",EDGE,"E64")}),-1.0]])]});
            var Q14;
            Q14=makeQuery(id+"F12.imprint","IMPRINT",FACE,{"disambiguationData":[TD([[makeQuery(id+"F12.imprint","IMPRINT",EDGE,{"derivedFrom":sQuery(id+"F12.wireOp",EDGE,"E75")}),-1.0]])]});
            var Q15;
            Q15=makeQuery(id+"F12.imprint","IMPRINT",FACE,{"disambiguationData":[TD([[makeQuery(id+"F12.imprint","IMPRINT",EDGE,{"derivedFrom":sQuery(id+"F12.wireOp",EDGE,"E104")}),-1.0]])]});
            var Q16;
            Q16=makeQuery(id+"F12.imprint","IMPRINT",FACE,{"disambiguationData":[TD([[makeQuery(id+"F12.imprint","IMPRINT",EDGE,{"derivedFrom":sQuery(id+"F12.wireOp",EDGE,"E94")}),-1.0]])]});
            var Q17;
            Q17=makeQuery(id+"F12.imprint","IMPRINT",FACE,{"disambiguationData":[TD([[makeQuery(id+"F12.imprint","IMPRINT",EDGE,{"derivedFrom":sQuery(id+"F12.wireOp",EDGE,"E88")}),-1.0]])]});
            var Q18;
            Q18=makeQuery(id+"F12.imprint","IMPRINT",FACE,{"disambiguationData":[TD([[makeQuery(id+"F12.imprint","IMPRINT",EDGE,{"derivedFrom":sQuery(id+"F12.wireOp",EDGE,"E91")}),-1.0]])]});
            var Q19;
            Q19=makeQuery(id+"F12.imprint","IMPRINT",FACE,{"disambiguationData":[TD([[makeQuery(id+"F12.imprint","IMPRINT",EDGE,{"derivedFrom":sQuery(id+"F12.wireOp",EDGE,"E97")}),-1.0]])]});
            var Q20;
            Q20=makeQuery(id+"F12.imprint","IMPRINT",FACE,{"disambiguationData":[TD([[makeQuery(id+"F12.imprint","IMPRINT",EDGE,{"derivedFrom":sQuery(id+"F12.wireOp",EDGE,"E81")}),-1.0]])]});
            var Q21;
            Q21=makeQuery(id+"F12.imprint","IMPRINT",FACE,{"disambiguationData":[TD([[makeQuery(id+"F12.imprint","IMPRINT",EDGE,{"derivedFrom":sQuery(id+"F12.wireOp",EDGE,"E78")}),-1.0]])]});
            var Q22;
            Q22=makeQuery(id+"F12.imprint","IMPRINT",FACE,{"disambiguationData":[TD([[makeQuery(id+"F12.imprint","IMPRINT",EDGE,{"derivedFrom":sQuery(id+"F12.wireOp",EDGE,"E84")}),-1.0]])]});
            var Q23;
            Q23=makeQuery(id+"F12.imprint","IMPRINT",FACE,{"disambiguationData":[TD([[makeQuery(id+"F12.imprint","IMPRINT",EDGE,{"derivedFrom":sQuery(id+"F12.wireOp",EDGE,"E101")}),-1.0]])]});
            extrude(context, id + "F14", {"entities" : qUnion([Q0, Q1, Q2, Q3, Q4, Q5, Q6, Q7, Q8, Q9, Q10, Q11, Q12, Q13, Q14, Q15, Q16, Q17, Q18, Q19, Q20, Q21, Q22, Q23]), "operationType" : NewBodyOperationType.REMOVE, "depth" : 3 * mm, "offsetDistance" : 25 * mm});
        }
    });
